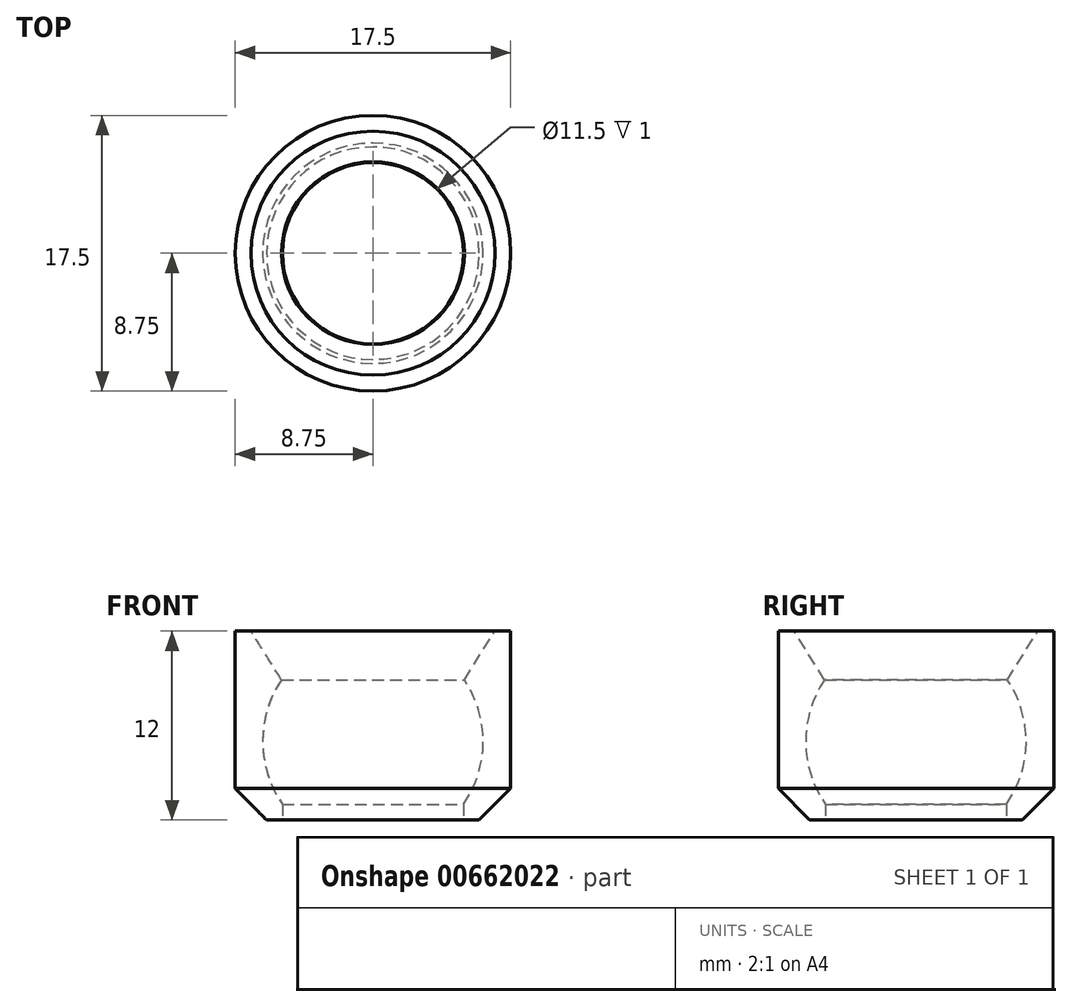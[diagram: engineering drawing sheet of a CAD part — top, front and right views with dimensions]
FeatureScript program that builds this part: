
annotation { "Feature Type Name" : "Feature", "Feature Type Description" : "" }
export const myFeature = defineFeature(function(context is Context, id is Id, definition is map)
    precondition{}
    {
        {
            var Q0;
            Q0=qCreatedBy(makeId("Front.planeOp"),FACE);
            var sketch = newSketch(context, id + "F0", { "sketchPlane" : qUnion([Q0])});
            skArc(sketch, "E0", {"start": v(-5.8, 8.9) * mm, "mid": v(-7, 4.94) * mm, "end": v(-5.75, 1) * mm});
            skLineSegment(sketch, "E1", {"start": v(0, 0) * mm, "end": v(0, 9.98) * mm, "construction": true});
            skLineSegment(sketch, "E2", {"start": v(-5.75, 0) * mm, "end": v(-5.75, 1) * mm});
            skLineSegment(sketch, "E3", {"start": v(-5.75, 0) * mm, "end": v(-6.75, 0) * mm});
            skLineSegment(sketch, "E4", {"start": v(-6.75, 0) * mm, "end": v(-8.75, 2) * mm});
            skLineSegment(sketch, "E5", {"start": v(-8.75, 2) * mm, "end": v(-8.75, 12) * mm});
            skLineSegment(sketch, "E6", {"start": v(-8.75, 12) * mm, "end": v(-7.75, 12) * mm});
            skLineSegment(sketch, "E7", {"start": v(-7.75, 12) * mm, "end": v(-5.8, 8.9) * mm});
            skSolve(sketch);
        }
        {
            var Q0;
            Q0 = qSketchRegion(id + "F0", true);
            var Q1;
            Q1=sQuery(id+"F0.wireOp",EDGE,"E1");
            revolve(context, id + "F1", {"entities" : qUnion([Q0]), "axis" : qUnion([Q1]), "revolveType" : RevolveType.FULL});
        }
    });
